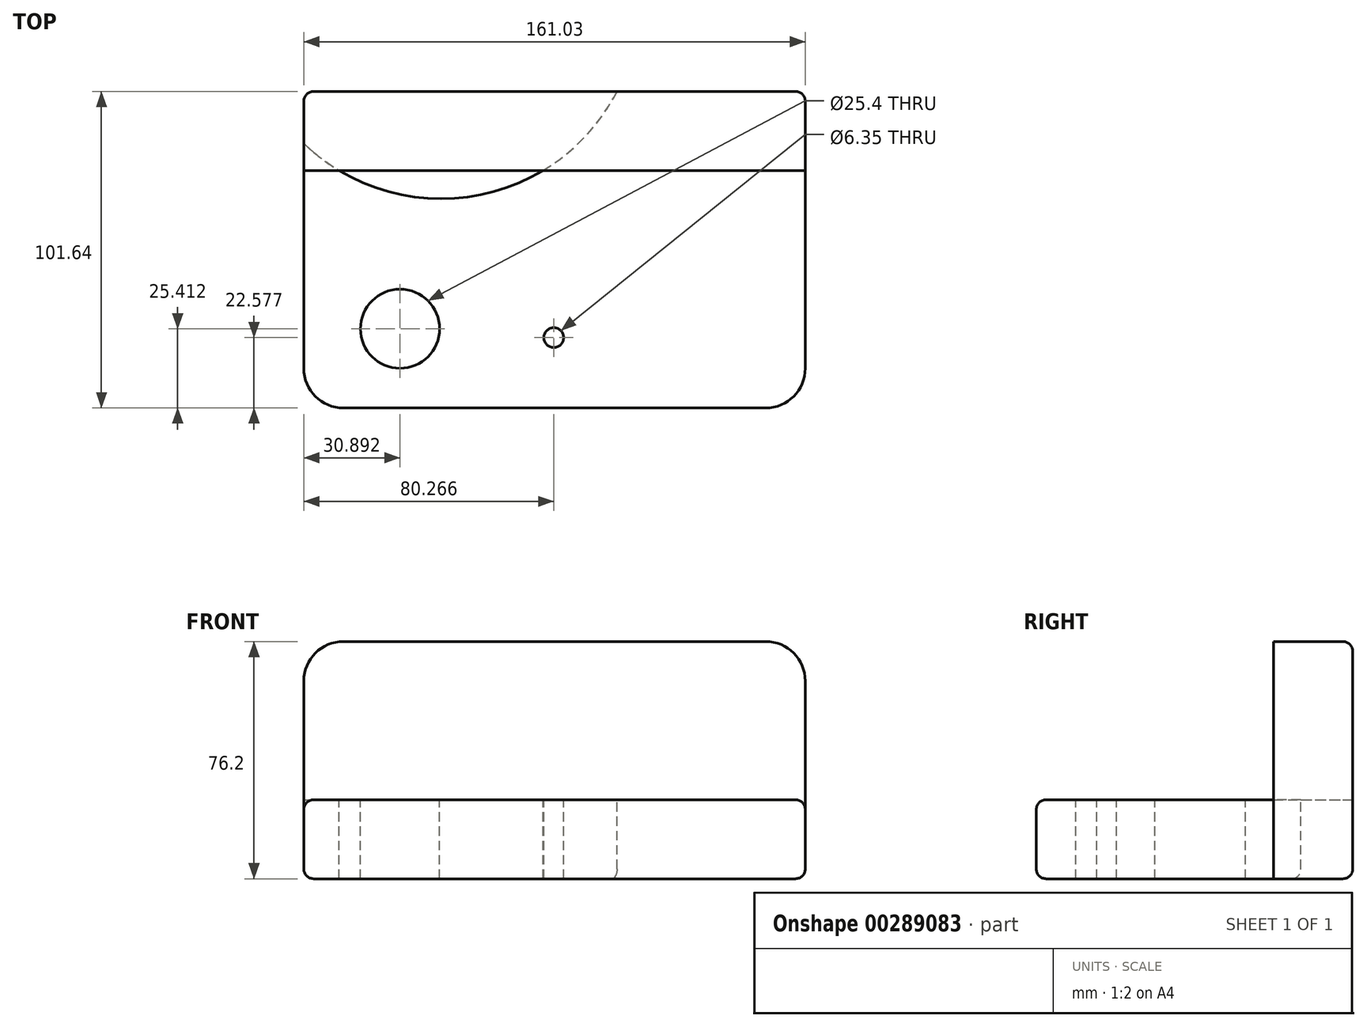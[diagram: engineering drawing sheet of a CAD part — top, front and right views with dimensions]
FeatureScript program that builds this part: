
annotation { "Feature Type Name" : "Feature", "Feature Type Description" : "" }
export const myFeature = defineFeature(function(context is Context, id is Id, definition is map)
    precondition{}
    {
        {
            var Q0;
            Q0=qCreatedBy(makeId("Top.planeOp"),FACE);
            var sketch = newSketch(context, id + "F0", { "sketchPlane" : qUnion([Q0])});
            skLineSegment(sketch, "E0.bottom", {"start": v(-115.52, 9.27) * mm, "end": v(45.5, 9.27) * mm});
            skLineSegment(sketch, "E0.top", {"start": v(-115.52, -66.97) * mm, "end": v(45.5, -66.97) * mm});
            skLineSegment(sketch, "E0.left", {"start": v(-115.52, 9.27) * mm, "end": v(-115.52, -66.97) * mm});
            skLineSegment(sketch, "E0.right", {"start": v(45.5, 9.27) * mm, "end": v(45.5, -66.97) * mm});
            skSolve(sketch);
        }
        {
            var Q0;
            Q0=makeQuery(id+"F0.imprint","IMPRINT",FACE,{"disambiguationData":[TD([[makeQuery(id+"F0.imprint","IMPRINT",EDGE,{"derivedFrom":sQuery(id+"F0.wireOp",EDGE,"E0.bottom")}),-1.0]])]});
            extrude(context, id + "F1", {"entities" : qUnion([Q0]), "depth" : 25.4 * mm});
        }
        {
            var Q0;
            Q0=makeQuery(id+"F1.opExtrude","CAP_FACE",FACE,{"disambiguationData":[OSD([sQuery(id+"F0.wireOp",EDGE,"E0.bottom"),sQuery(id+"F0.wireOp",EDGE,"E0.top"),sQuery(id+"F0.wireOp",EDGE,"E0.left"),sQuery(id+"F0.wireOp",EDGE,"E0.right")])],"isStart":false});
            var sketch = newSketch(context, id + "F2", { "sketchPlane" : qUnion([Q0])});
            skLineSegment(sketch, "E1", {"start": v(-115.52, 9.27) * mm, "end": v(45.5, 9.27) * mm});
            skLineSegment(sketch, "E2", {"start": v(45.5, 9.27) * mm, "end": v(45.5, 34.67) * mm});
            skLineSegment(sketch, "E3", {"start": v(45.5, 34.67) * mm, "end": v(-115.52, 34.67) * mm});
            skLineSegment(sketch, "E4", {"start": v(-115.52, 34.67) * mm, "end": v(-115.52, 9.27) * mm});
            skSolve(sketch);
        }
        {
            var Q0;
            Q0 = qSketchRegion(id + "F2", true);
            extrude(context, id + "F3", {"entities" : qUnion([Q0]), "depth" : 50.8 * mm, "hasSecondDirection" : true, "secondDirectionOppositeDirection" : true, "secondDirectionDepth" : 25.4 * mm});
        }
        {
            var Q0;
            Q0=makeQuery(id+"F1.opExtrude","CAP_FACE",FACE,{"disambiguationData":[OSD([sQuery(id+"F0.wireOp",EDGE,"E0.bottom"),sQuery(id+"F0.wireOp",EDGE,"E0.top"),sQuery(id+"F0.wireOp",EDGE,"E0.left"),sQuery(id+"F0.wireOp",EDGE,"E0.right")])],"isStart":false});
            var sketch = newSketch(context, id + "F4", { "sketchPlane" : qUnion([Q0])});
            skCircle(sketch, "E5", {"center": v(-84.63, -41.56) * mm, "radius": 10.94 * mm});
            skCircle(sketch, "E6", {"center": v(-71.43, 63.68) * mm, "radius": 74.32 * mm});
            skSolve(sketch);
        }
        {
            var Q0;
            Q0=sQuery(id+"F4.wireOp",VERTEX,"E5.center");
            var Q1;
            Q1=makeQuery(id+"F1.opExtrude","SWEPT_BODY",BODY,{"disambiguationData":[OSD([sQuery(id+"F0.wireOp",EDGE,"E0.bottom"),sQuery(id+"F0.wireOp",EDGE,"E0.top"),sQuery(id+"F0.wireOp",EDGE,"E0.left"),sQuery(id+"F0.wireOp",EDGE,"E0.right")])]});
            hole(context, id + "F5", {"style" : HoleStyle.SIMPLE, "endStyle" : HoleEndStyle.THROUGH, "holeDiameter" : 25.4 * mm, "tappedDepth" : 12.7 * mm, "tapClearance" : 3, "locations" : qUnion([Q0]), "scope" : qUnion([Q1])});
        }
        {
            var Q0;
            Q0=sQuery(id+"F4.wireOp",VERTEX,"E6.center");
            var Q1;
            Q1=makeQuery(id+"F1.opExtrude","SWEPT_BODY",BODY,{"disambiguationData":[OSD([sQuery(id+"F0.wireOp",EDGE,"E0.bottom"),sQuery(id+"F0.wireOp",EDGE,"E0.top"),sQuery(id+"F0.wireOp",EDGE,"E0.left"),sQuery(id+"F0.wireOp",EDGE,"E0.right")])]});
            var Q2;
            Q2=makeQuery(id+"F3.opExtrude","SWEPT_BODY",BODY,{"disambiguationData":[OSD([sQuery(id+"F2.wireOp",EDGE,"E1"),sQuery(id+"F2.wireOp",EDGE,"E2"),sQuery(id+"F2.wireOp",EDGE,"E3"),sQuery(id+"F2.wireOp",EDGE,"E4")])]});
            hole(context, id + "F6", {"style" : HoleStyle.SIMPLE, "endStyle" : HoleEndStyle.THROUGH, "holeDiameter" : 127 * mm, "tappedDepth" : 12.7 * mm, "tapClearance" : 3, "locations" : qUnion([Q0]), "scope" : qUnion([Q1, Q2])});
        }
        {
            var Q0;
            Q0=makeQuery(id+"F1.opExtrude","SWEPT_EDGE",EDGE,{"disambiguationData":[OSD([sQuery(id+"F0.wireOp",EDGE,"E0.top"),sQuery(id+"F0.wireOp",EDGE,"E0.left")])]});
            var Q1;
            Q1=makeQuery(id+"F1.opExtrude","SWEPT_EDGE",EDGE,{"disambiguationData":[OSD([sQuery(id+"F0.wireOp",EDGE,"E0.top"),sQuery(id+"F0.wireOp",EDGE,"E0.right")])]});
            fillet(context, id + "F7", {"entities" : qUnion([Q0, Q1]), "radius" : 12.7 * mm, "tangentPropagation" : true, "allowEdgeOverflow" : false});
        }
        {
            var Q0;
            Q0=makeQuery(id+"F3.opExtrude","CAP_EDGE",EDGE,{"disambiguationData":[OSD([sQuery(id+"F2.wireOp",EDGE,"E4")])],"isStart":false});
            var Q1;
            Q1=makeQuery(id+"F3.opExtrude","CAP_EDGE",EDGE,{"disambiguationData":[OSD([sQuery(id+"F2.wireOp",EDGE,"E2")])],"isStart":false});
            fillet(context, id + "F8", {"entities" : qUnion([Q0, Q1]), "radius" : 12.7 * mm, "tangentPropagation" : true, "defaultsChanged" : true, "vertexSettings" : [], "allowEdgeOverflow" : false});
        }
        {
            var Q0;
            Q0=makeQuery(id+"F1.opExtrude","CAP_EDGE",EDGE,{"disambiguationData":[OSD([sQuery(id+"F0.wireOp",EDGE,"E0.left")])],"isStart":false});
            var Q1;
            Q1=makeQuery(id+"F1.opExtrude","CAP_EDGE",EDGE,{"disambiguationData":[OSD([sQuery(id+"F0.wireOp",EDGE,"E0.right")])],"isStart":true});
            var Q2;
            Q2=makeQuery(id+"F3.opExtrude","CAP_EDGE",EDGE,{"disambiguationData":[OSD([sQuery(id+"F2.wireOp",EDGE,"E4")])],"isStart":true});
            var Q3;
            Q3=makeQuery(id+"F3.opExtrude","CAP_EDGE",EDGE,{"disambiguationData":[OSD([sQuery(id+"F2.wireOp",EDGE,"E2")])],"isStart":true});
            var Q4;
            Q4=makeQuery(id+"F3.opExtrude","SWEPT_EDGE",EDGE,{"disambiguationData":[OSD([sQuery(id+"F2.wireOp",EDGE,"E2"),sQuery(id+"F2.wireOp",EDGE,"E3")])]});
            var Q5;
            Q5=makeQuery(id+"F3.opExtrude","CAP_EDGE",EDGE,{"disambiguationData":[OSD([sQuery(id+"F2.wireOp",EDGE,"E3")])],"isStart":true});
            var Q6;
            Q6=makeQuery(id+"F6.hole-0.boolean.opBoolean","INTERSECT",EDGE,{"disambiguationData":[OD(0.0)],"derivedFrom":[makeQuery(id+"F3.opExtrude","CAP_FACE",FACE,{"disambiguationData":[OSD([sQuery(id+"F2.wireOp",EDGE,"E1"),sQuery(id+"F2.wireOp",EDGE,"E2"),sQuery(id+"F2.wireOp",EDGE,"E3"),sQuery(id+"F2.wireOp",EDGE,"E4")])],"isStart":true}),makeQuery(id+"F6.hole-0.opRevolve","SWEPT_FACE",FACE,{"disambiguationData":[OSD([sQuery(id+"F6.hole-0.sketch.wireOp",EDGE,"core_line_2")])]})]});
            var Q7;
            Q7=makeQuery(id+"F6.hole-0.boolean.opBoolean","INTERSECT",EDGE,{"derivedFrom":[makeQuery(id+"F1.opExtrude","CAP_FACE",FACE,{"disambiguationData":[OSD([sQuery(id+"F0.wireOp",EDGE,"E0.bottom"),sQuery(id+"F0.wireOp",EDGE,"E0.top"),sQuery(id+"F0.wireOp",EDGE,"E0.left"),sQuery(id+"F0.wireOp",EDGE,"E0.right")])],"isStart":true}),makeQuery(id+"F6.hole-0.opRevolve","SWEPT_FACE",FACE,{"disambiguationData":[OSD([sQuery(id+"F6.hole-0.sketch.wireOp",EDGE,"core_line_2")])]})]});
            var Q8;
            Q8=makeQuery(id+"F6.hole-0.boolean.opBoolean","INTERSECT",EDGE,{"disambiguationData":[OD(1.0)],"derivedFrom":[makeQuery(id+"F3.opExtrude","CAP_FACE",FACE,{"disambiguationData":[OSD([sQuery(id+"F2.wireOp",EDGE,"E1"),sQuery(id+"F2.wireOp",EDGE,"E2"),sQuery(id+"F2.wireOp",EDGE,"E3"),sQuery(id+"F2.wireOp",EDGE,"E4")])],"isStart":true}),makeQuery(id+"F6.hole-0.opRevolve","SWEPT_FACE",FACE,{"disambiguationData":[OSD([sQuery(id+"F6.hole-0.sketch.wireOp",EDGE,"core_line_2")])]})]});
            fillet(context, id + "F9", {"entities" : qUnion([Q0, Q1, Q2, Q3, Q4, Q5, Q6, Q7, Q8]), "radius" : 3.17 * mm, "tangentPropagation" : true, "allowEdgeOverflow" : false});
        }
        {
            var Q0;
            Q0=makeQuery(id+"F1.opExtrude","CAP_FACE",FACE,{"disambiguationData":[OSD([sQuery(id+"F0.wireOp",EDGE,"E0.bottom"),sQuery(id+"F0.wireOp",EDGE,"E0.top"),sQuery(id+"F0.wireOp",EDGE,"E0.left"),sQuery(id+"F0.wireOp",EDGE,"E0.right")])],"isStart":false});
            var sketch = newSketch(context, id + "F10", { "sketchPlane" : qUnion([Q0])});
            skCircle(sketch, "E7", {"center": v(-35.25, -44.4) * mm, "radius": 9.8 * mm});
            skSolve(sketch);
        }
        {
            var Q0;
            Q0=sQuery(id+"F10.wireOp",VERTEX,"E7.center");
            var Q1;
            Q1=makeQuery(id+"F1.opExtrude","SWEPT_BODY",BODY,{"disambiguationData":[OSD([sQuery(id+"F0.wireOp",EDGE,"E0.bottom"),sQuery(id+"F0.wireOp",EDGE,"E0.top"),sQuery(id+"F0.wireOp",EDGE,"E0.left"),sQuery(id+"F0.wireOp",EDGE,"E0.right")])]});
            hole(context, id + "F11", {"style" : HoleStyle.SIMPLE, "endStyle" : HoleEndStyle.THROUGH, "holeDiameter" : 6.35 * mm, "majorDiameter" : 6.35 * mm, "isTappedThrough" : true, "tappedDepth" : 12.7 * mm, "tapClearance" : 3, "locations" : qUnion([Q0]), "scope" : qUnion([Q1])});
        }
    });
